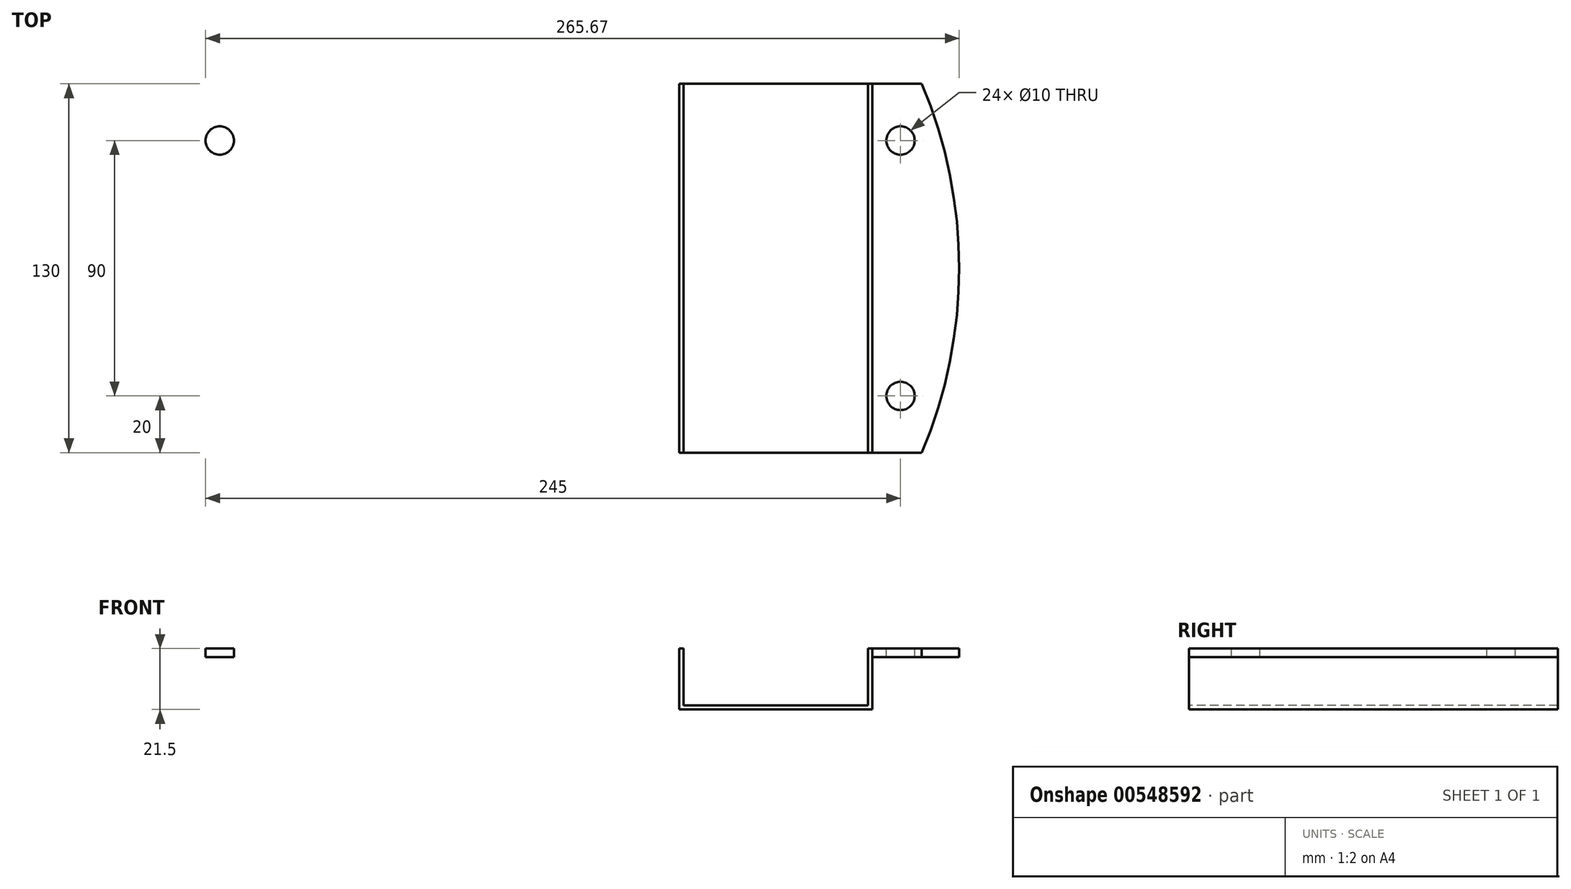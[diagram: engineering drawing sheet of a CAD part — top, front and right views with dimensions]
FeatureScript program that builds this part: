
annotation { "Feature Type Name" : "Feature", "Feature Type Description" : "" }
export const myFeature = defineFeature(function(context is Context, id is Id, definition is map)
    precondition{}
    {
        {
            var Q0;
            Q0=qCreatedBy(makeId("Top.planeOp"),FACE);
            var sketch = newSketch(context, id + "F0", { "sketchPlane" : qUnion([Q0])});
            skPoint(sketch, "E0.middle", {"position": v(0, 0) * mm});
            skArc(sketch, "E1", {"start": v(127.5, -65) * mm, "mid": v(140.67, 0) * mm, "end": v(127.5, 65) * mm});
            skArc(sketch, "E2.MirrorCS", {"start": v(-127.5, -65) * mm, "mid": v(-140.67, 0) * mm, "end": v(-127.5, 65) * mm});
            skCircle(sketch, "E3", {"center": v(120, 45) * mm, "radius": 5 * mm});
            skCircle(sketch, "E4.MirrorC", {"center": v(120, -45) * mm, "radius": 5 * mm});
            skCircle(sketch, "E5.MirrorC", {"center": v(-120, 45) * mm, "radius": 5 * mm});
            skCircle(sketch, "E6.MirrorC", {"center": v(-120, -45) * mm, "radius": 5 * mm});
            skCircle(sketch, "E7", {"center": v(-120, 20) * mm, "radius": 2 * mm});
            skCircle(sketch, "E8.MirrorC", {"center": v(-120, -20) * mm, "radius": 2 * mm});
            skLineSegment(sketch, "E9", {"start": v(-127.5, 65) * mm, "end": v(42, 65) * mm});
            skLineSegment(sketch, "E10.MirrorCS", {"start": v(-127.5, -65) * mm, "end": v(42, -65) * mm});
            skLineSegment(sketch, "E11.left", {"start": v(42, 65) * mm, "end": v(42, -65) * mm});
            skLineSegment(sketch, "E11.right", {"start": v(110, 65) * mm, "end": v(110, -65) * mm});
            skLineSegment(sketch, "E12.trimOffspring", {"start": v(110, 65) * mm, "end": v(127.5, 65) * mm});
            skLineSegment(sketch, "E13.trimOffspring", {"start": v(110, -65) * mm, "end": v(127.5, -65) * mm});
            skLineSegment(sketch, "E14", {"start": v(42, 65) * mm, "end": v(110, 65) * mm});
            skLineSegment(sketch, "E15", {"start": v(42, -65) * mm, "end": v(110, -65) * mm});
            skCircle(sketch, "E16.MirrorC", {"center": v(-53, 45) * mm, "radius": 5 * mm});
            skCircle(sketch, "E17.MirrorC", {"center": v(32, 45) * mm, "radius": 5 * mm});
            skCircle(sketch, "E18.MirrorC", {"center": v(32, -45) * mm, "radius": 5 * mm});
            skCircle(sketch, "E19.MirrorC", {"center": v(-53, -45) * mm, "radius": 5 * mm});
            skSolve(sketch);
        }
        {
            var Q0;
            Q0=makeQuery(id+"F0.imprint","IMPRINT",FACE,{"disambiguationData":[TD([[makeQuery(id+"F0.imprint","IMPRINT",EDGE,{"derivedFrom":sQuery(id+"F0.wireOp",EDGE,"E5.MirrorC")}),1.0]])]});
            var Q1;
            Q1=makeQuery(id+"F0.imprint","IMPRINT",FACE,{"disambiguationData":[TD([[makeQuery(id+"F0.imprint","IMPRINT",EDGE,{"derivedFrom":sQuery(id+"F0.wireOp",EDGE,"E1")}),1.0]])]});
            var Q2;
            Q2=makeQuery(id+"F0.imprint","IMPRINT",FACE,{"disambiguationData":[TD([[makeQuery(id+"F0.imprint","IMPRINT",EDGE,{"derivedFrom":sQuery(id+"F0.wireOp",EDGE,"E2.MirrorCS")}),-1.0]])]});
            extrude(context, id + "F1", {"entities" : qUnion([Q0, Q1, Q2]), "oppositeDirection" : true, "depth" : 3 * mm, "offsetDistance" : 25 * mm});
        }
        {
            var Q0;
            Q0=makeQuery(id+"F0.imprint","IMPRINT",FACE,{"disambiguationData":[TD([[makeQuery(id+"F0.imprint","IMPRINT",EDGE,{"derivedFrom":sQuery(id+"F0.wireOp",EDGE,"E11.left")}),1.0]])]});
            extrude(context, id + "F2", {"entities" : qUnion([Q0]), "oppositeDirection" : true, "depth" : 21.5 * mm, "offsetDistance" : 25 * mm});
        }
        {
            var Q0;
            Q0=makeQuery(id+"F2.opExtrude","SWEPT_FACE",FACE,{"disambiguationData":[OSD([sQuery(id+"F0.wireOp",EDGE,"E15")])]});
            var Q1;
            Q1=makeQuery(id+"F2.opExtrude","SWEPT_FACE",FACE,{"disambiguationData":[OSD([sQuery(id+"F0.wireOp",EDGE,"E14")])]});
            var Q2;
            Q2=makeQuery(id+"F2.opExtrude","CAP_FACE",FACE,{"disambiguationData":[OSD([sQuery(id+"F0.wireOp",EDGE,"E11.left"),sQuery(id+"F0.wireOp",EDGE,"E11.right"),sQuery(id+"F0.wireOp",EDGE,"E14"),sQuery(id+"F0.wireOp",EDGE,"E15")])],"isStart":true});
            shell(context, id + "F3", {"entities" : qUnion([Q0, Q1, Q2]), "thickness" : 1.5 * mm});
        }
    });
